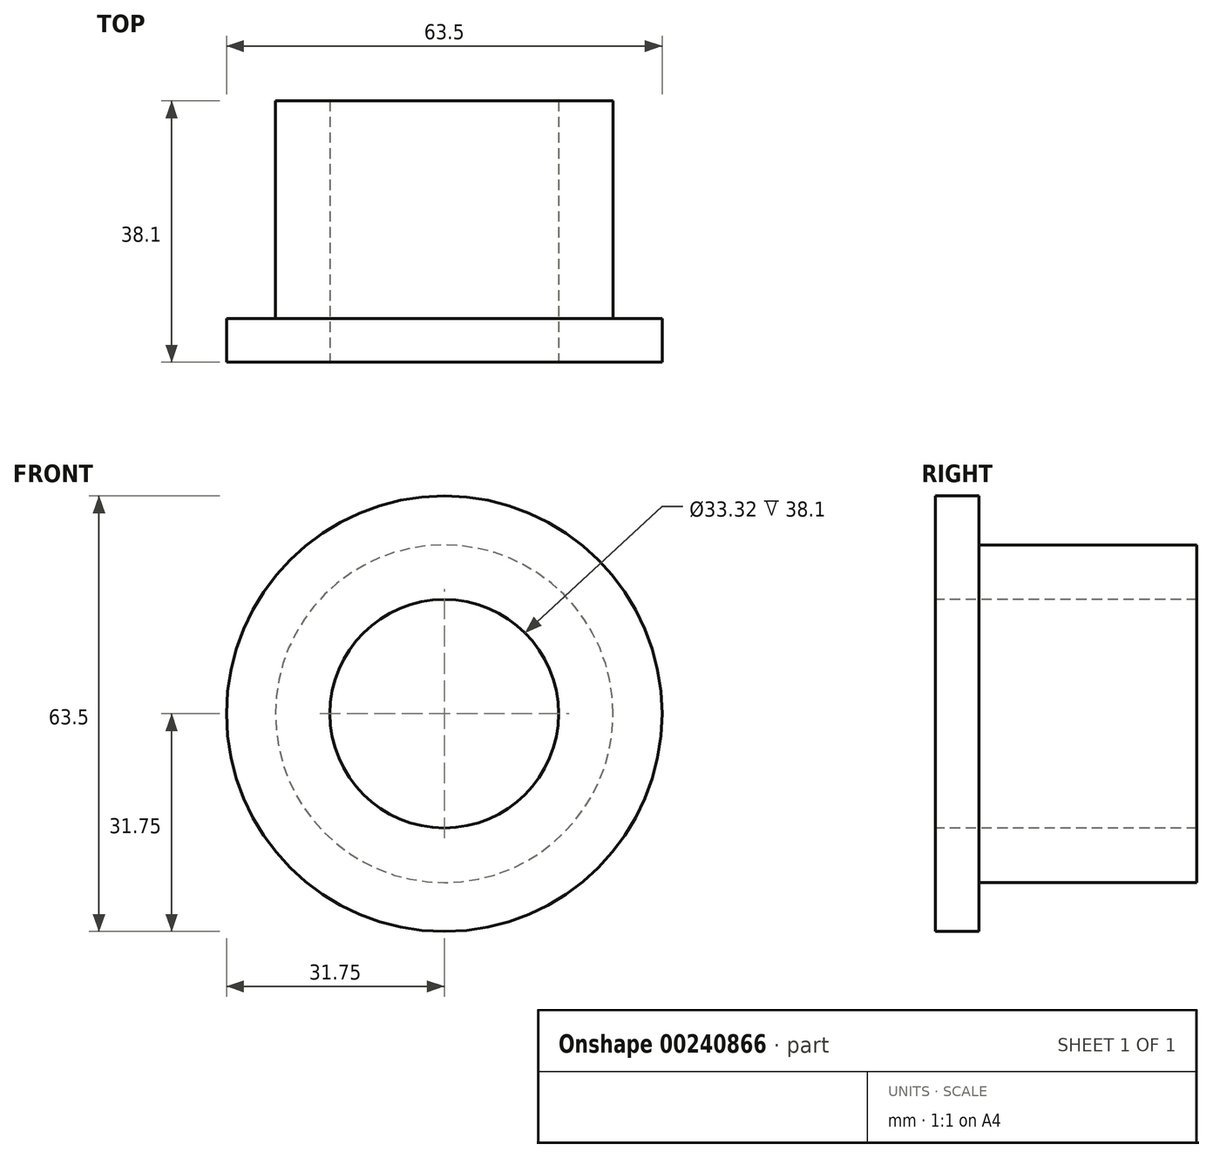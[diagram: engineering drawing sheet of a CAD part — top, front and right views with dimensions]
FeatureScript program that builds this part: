
annotation { "Feature Type Name" : "Feature", "Feature Type Description" : "" }
export const myFeature = defineFeature(function(context is Context, id is Id, definition is map)
    precondition{}
    {
        {
            var Q0;
            Q0=qCreatedBy(makeId("Front.planeOp"),FACE);
            var sketch = newSketch(context, id + "F0", { "sketchPlane" : qUnion([Q0])});
            skCircle(sketch, "E0", {"center": v(0, 0) * mm, "radius": 16.66 * mm});
            skCircle(sketch, "E1", {"center": v(0, 0) * mm, "radius": 24.61 * mm});
            skSolve(sketch);
        }
        {
            var Q0;
            Q0=makeQuery(id+"F0.imprint","IMPRINT",FACE,{"disambiguationData":[TD([[makeQuery(id+"F0.imprint","IMPRINT",EDGE,{"derivedFrom":sQuery(id+"F0.wireOp",EDGE,"E0")}),-1.0]])]});
            extrude(context, id + "F1", {"entities" : qUnion([Q0]), "oppositeDirection" : true, "depth" : 31.75 * mm});
        }
        {
            var Q0;
            Q0=qCreatedBy(makeId("Front.planeOp"),FACE);
            var sketch = newSketch(context, id + "F2", { "sketchPlane" : qUnion([Q0])});
            skCircle(sketch, "E2", {"center": v(0, 0) * mm, "radius": 16.66 * mm});
            skCircle(sketch, "E3", {"center": v(0, 0) * mm, "radius": 31.75 * mm});
            skSolve(sketch);
        }
        {
            var Q0;
            Q0 = qSketchRegion(id + "F2", true);
            extrude(context, id + "F3", {"entities" : qUnion([Q0]), "operationType" : NewBodyOperationType.ADD, "depth" : 6.35 * mm});
        }
    });
